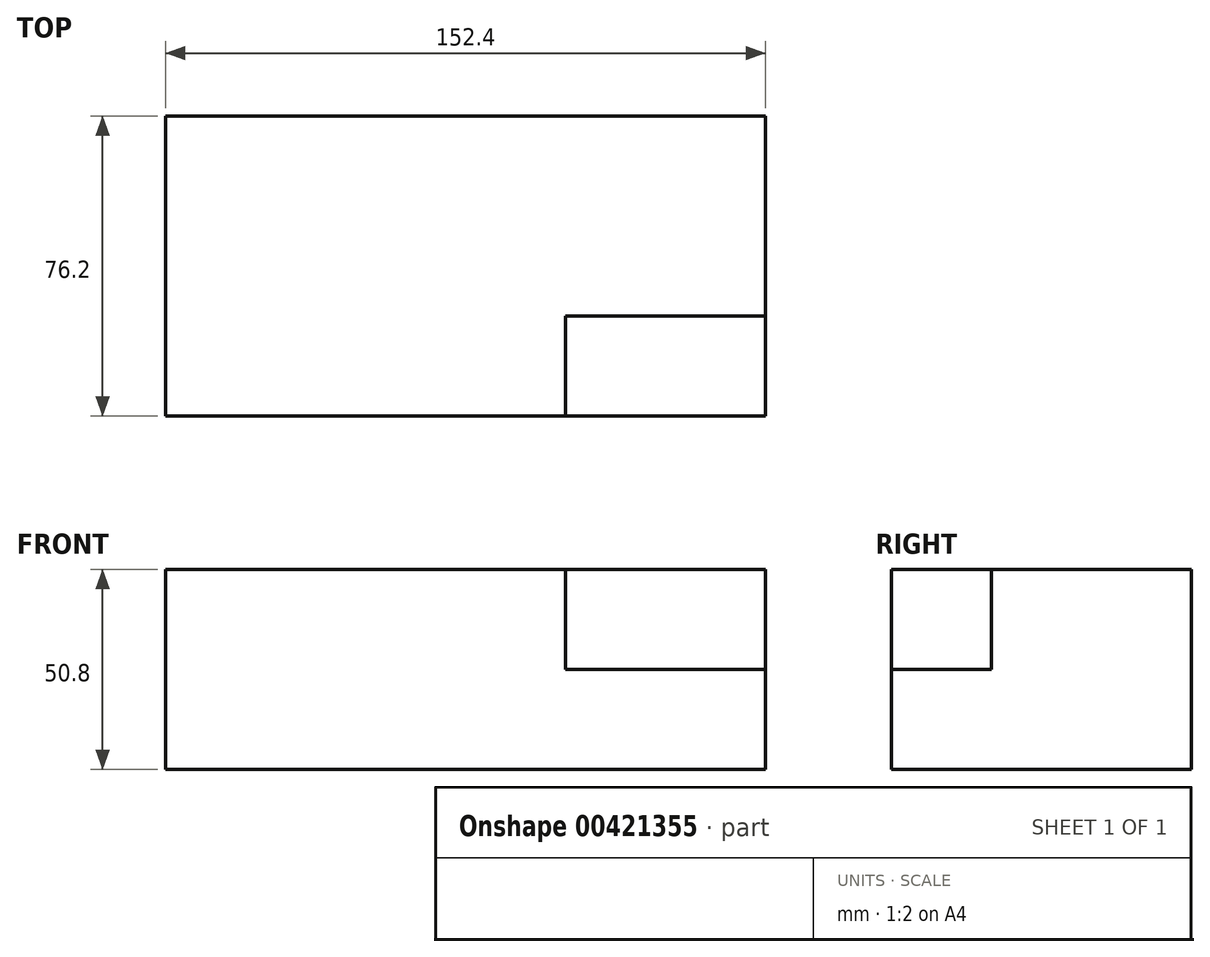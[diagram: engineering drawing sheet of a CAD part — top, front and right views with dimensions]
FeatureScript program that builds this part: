
annotation { "Feature Type Name" : "Feature", "Feature Type Description" : "" }
export const myFeature = defineFeature(function(context is Context, id is Id, definition is map)
    precondition{}
    {
        {
            var Q0;
            Q0=qCreatedBy(makeId("Front.planeOp"),FACE);
            var sketch = newSketch(context, id + "F0", { "sketchPlane" : qUnion([Q0])});
            skLineSegment(sketch, "E0", {"start": v(0, 0) * mm, "end": v(152.4, 0) * mm});
            skLineSegment(sketch, "E1", {"start": v(152.4, 0) * mm, "end": v(152.4, 50.8) * mm});
            skLineSegment(sketch, "E2", {"start": v(152.4, 50.8) * mm, "end": v(0, 50.8) * mm});
            skLineSegment(sketch, "E3", {"start": v(0, 50.8) * mm, "end": v(0, 0) * mm});
            skSolve(sketch);
        }
        {
            var Q0;
            Q0=makeQuery(id+"F0.imprint","IMPRINT",FACE,{"disambiguationData":[TD([[makeQuery(id+"F0.imprint","IMPRINT",EDGE,{"derivedFrom":sQuery(id+"F0.wireOp",EDGE,"E0")}),1.0]])]});
            extrude(context, id + "F1", {"entities" : qUnion([Q0]), "depth" : 76.2 * mm});
        }
        {
            var Q0;
            Q0=makeQuery(id+"F1.opExtrude","CAP_FACE",FACE,{"disambiguationData":[OSD([sQuery(id+"F0.wireOp",EDGE,"E0"),sQuery(id+"F0.wireOp",EDGE,"E1"),sQuery(id+"F0.wireOp",EDGE,"E2"),sQuery(id+"F0.wireOp",EDGE,"E3")])],"isStart":false});
            var Q1;
            Q1=makeQuery(id+"F1.opExtrude","CAP_FACE",FACE,{"disambiguationData":[OSD([sQuery(id+"F0.wireOp",EDGE,"E0"),sQuery(id+"F0.wireOp",EDGE,"E1"),sQuery(id+"F0.wireOp",EDGE,"E2"),sQuery(id+"F0.wireOp",EDGE,"E3")])],"isStart":true});
            extrude(context, id + "F2", {"entities" : qUnion([Q0, Q1]), "operationType" : NewBodyOperationType.ADD, "depth" : 25.4 * mm});
        }
        {
            var Q0;
            {var subQ0=sQuery(id+"F0.wireOp",EDGE,"E3");var subQ1=sQuery(id+"F0.wireOp",EDGE,"E2");var subQ2=sQuery(id+"F0.wireOp",EDGE,"E1");var subQ3=sQuery(id+"F0.wireOp",EDGE,"E0");Q0=makeQuery(id+"F2.opExtrude","CAP_FACE",FACE,{"disambiguationData":[OSD([subQ3,subQ2,subQ1,subQ0]),TDD([makeQuery(id+"F1.opExtrude","CAP_FACE",FACE,{"disambiguationData":[OSD([subQ3,subQ2,subQ1,subQ0])],"isStart":false})])],"isStart":false});}
            var sketch = newSketch(context, id + "F3", { "sketchPlane" : qUnion([Q0])});
            skLineSegment(sketch, "E4", {"start": v(152.4, 25.4) * mm, "end": v(101.6, 25.4) * mm});
            skLineSegment(sketch, "E5", {"start": v(101.6, 25.4) * mm, "end": v(101.6, 50.8) * mm});
            skLineSegment(sketch, "E6", {"start": v(101.6, 50.8) * mm, "end": v(152.4, 50.8) * mm});
            skLineSegment(sketch, "E7", {"start": v(152.4, 50.8) * mm, "end": v(152.4, 25.4) * mm});
            skSolve(sketch);
        }
        {
            var Q0;
            Q0=makeQuery(id+"F3.imprint","IMPRINT",FACE,{"disambiguationData":[TD([[makeQuery(id+"F3.imprint","IMPRINT",EDGE,{"derivedFrom":sQuery(id+"F3.wireOp",EDGE,"E4")}),-1.0]])]});
            extrude(context, id + "F4", {"entities" : qUnion([Q0]), "operationType" : NewBodyOperationType.REMOVE, "oppositeDirection" : true, "depth" : 25.4 * mm});
        }
        {
            var Q0;
            {var subQ0=sQuery(id+"F0.wireOp",EDGE,"E3");var subQ1=sQuery(id+"F0.wireOp",EDGE,"E2");var subQ2=sQuery(id+"F0.wireOp",EDGE,"E1");var subQ3=sQuery(id+"F0.wireOp",EDGE,"E0");Q0=makeQuery(id+"F2.opExtrude","CAP_FACE",FACE,{"disambiguationData":[OSD([subQ3,subQ2,subQ1,subQ0]),TDD([makeQuery(id+"F1.opExtrude","CAP_FACE",FACE,{"disambiguationData":[OSD([subQ3,subQ2,subQ1,subQ0])],"isStart":false})])],"isStart":false});}
            extrude(context, id + "F5", {"entities" : qUnion([Q0]), "operationType" : NewBodyOperationType.REMOVE, "oppositeDirection" : true, "depth" : 25.4 * mm});
        }
        {
            var Q0;
            Q0=makeQuery(id+"F5.boolean.opBoolean","MERGE",FACE,{"derivedFrom":[makeQuery(id+"F4.boolean.opBoolean","COPY",FACE,{"derivedFrom":makeQuery(id+"F4.opExtrude","CAP_FACE",FACE,{"disambiguationData":[OSD([sQuery(id+"F3.wireOp",EDGE,"E4"),sQuery(id+"F3.wireOp",EDGE,"E5"),sQuery(id+"F3.wireOp",EDGE,"E6"),sQuery(id+"F3.wireOp",EDGE,"E7")])],"isStart":false})}),makeQuery(id+"F5.opExtrude","CAP_FACE",FACE,{"disambiguationData":[OSD([sQuery(id+"F0.wireOp",EDGE,"E0"),sQuery(id+"F0.wireOp",EDGE,"E1"),sQuery(id+"F0.wireOp",EDGE,"E2"),sQuery(id+"F0.wireOp",EDGE,"E3")])],"isStart":false})]});
            var sketch = newSketch(context, id + "F6", { "sketchPlane" : qUnion([Q0])});
            skLineSegment(sketch, "E8", {"start": v(152.4, 25.4) * mm, "end": v(101.6, 25.4) * mm});
            skLineSegment(sketch, "E9", {"start": v(101.6, 25.4) * mm, "end": v(101.6, 50.8) * mm});
            skLineSegment(sketch, "E10", {"start": v(101.6, 50.8) * mm, "end": v(152.4, 50.8) * mm});
            skLineSegment(sketch, "E11", {"start": v(152.4, 50.8) * mm, "end": v(152.4, 25.4) * mm});
            skSolve(sketch);
        }
        {
            var Q0;
            Q0=makeQuery(id+"F6.imprint","IMPRINT",FACE,{"disambiguationData":[TD([[makeQuery(id+"F6.imprint","IMPRINT",EDGE,{"derivedFrom":sQuery(id+"F6.wireOp",EDGE,"E8")}),-1.0]])]});
            extrude(context, id + "F7", {"entities" : qUnion([Q0]), "operationType" : NewBodyOperationType.REMOVE, "oppositeDirection" : true, "depth" : 25.4 * mm});
        }
    });
